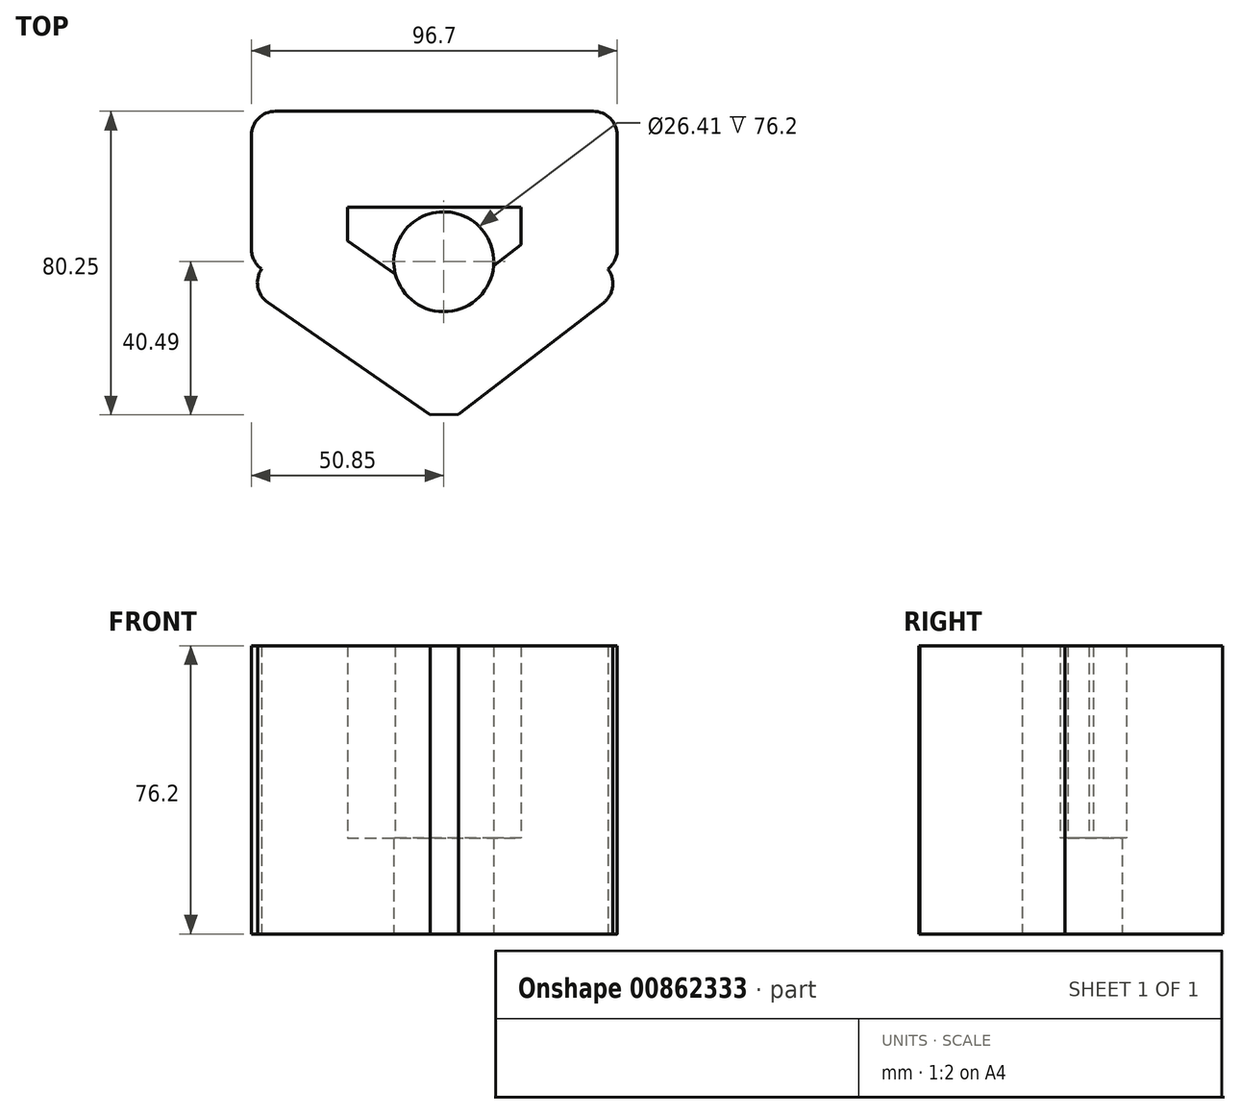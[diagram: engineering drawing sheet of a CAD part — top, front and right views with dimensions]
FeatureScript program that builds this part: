
annotation { "Feature Type Name" : "Feature", "Feature Type Description" : "" }
export const myFeature = defineFeature(function(context is Context, id is Id, definition is map)
    precondition{}
    {
        {
            var Q0;
            Q0=qCreatedBy(makeId("Top.planeOp"),FACE);
            var sketch = newSketch(context, id + "F0", { "sketchPlane" : qUnion([Q0])});
            skLineSegment(sketch, "E0", {"start": v(-44.5, 39.76) * mm, "end": v(39.5, 39.76) * mm});
            skLineSegment(sketch, "E1", {"start": v(-50.85, 33.4) * mm, "end": v(-50.85, 3.32) * mm});
            skPoint(sketch, "E2.visualSharp", {"position": v(-50.85, 39.76) * mm});
            skArc(sketch, "E2.filletArc", {"start": v(-44.5, 39.76) * mm, "mid": v(-48.99, 37.9) * mm, "end": v(-50.85, 33.4) * mm});
            skLineSegment(sketch, "E3", {"start": v(45.85, 33.4) * mm, "end": v(45.85, 3.13) * mm});
            skPoint(sketch, "E4.visualSharp", {"position": v(45.85, 39.76) * mm});
            skArc(sketch, "E4.filletArc", {"start": v(45.85, 33.4) * mm, "mid": v(44, 37.9) * mm, "end": v(39.5, 39.76) * mm});
            skLineSegment(sketch, "E5", {"start": v(-48.12, -1.9) * mm, "end": v(0, -35.27) * mm});
            skLineSegment(sketch, "E6", {"start": v(43.37, -1.9) * mm, "end": v(0, -35.27) * mm});
            skPoint(sketch, "E7.visualSharp", {"position": v(-50.85, 0) * mm});
            skArc(sketch, "E7.filletArc", {"start": v(-50.85, 3.32) * mm, "mid": v(-50.12, 0.38) * mm, "end": v(-48.12, -1.9) * mm});
            skPoint(sketch, "E8.visualSharp", {"position": v(45.85, 0) * mm});
            skArc(sketch, "E8.filletArc", {"start": v(43.37, -1.9) * mm, "mid": v(45.2, 0.32) * mm, "end": v(45.85, 3.13) * mm});
            skLineSegment(sketch, "E9.0", {"start": v(-46.52, -10.73) * mm, "end": v(-3.62, -40.49) * mm});
            skLineSegment(sketch, "E10", {"start": v(-48.12, -1.9) * mm, "end": v(-48.12, -1.9) * mm});
            skLineSegment(sketch, "E11", {"start": v(-3.62, -40.49) * mm, "end": v(0, -35.27) * mm});
            skLineSegment(sketch, "E12", {"start": v(0, -35.27) * mm, "end": v(3.73, -40.12) * mm});
            skLineSegment(sketch, "E13.0", {"start": v(42.21, -10.81) * mm, "end": v(3.87, -40.3) * mm});
            skCircle(sketch, "E14", {"center": v(0, 0) * mm, "radius": 13.2 * mm});
            skLineSegment(sketch, "E15", {"start": v(43.37, -1.9) * mm, "end": v(43.37, -1.9) * mm});
            skLineSegment(sketch, "E16", {"start": v(-3.62, -40.49) * mm, "end": v(3.87, -40.3) * mm});
            skPoint(sketch, "E17.visualSharp", {"position": v(-51.74, -7.11) * mm});
            skArc(sketch, "E17.filletArc", {"start": v(-48.12, -1.9) * mm, "mid": v(-49.15, -6.64) * mm, "end": v(-46.52, -10.73) * mm});
            skPoint(sketch, "E18.visualSharp", {"position": v(47.24, -6.94) * mm});
            skArc(sketch, "E18.filletArc", {"start": v(42.21, -10.81) * mm, "mid": v(44.64, -6.6) * mm, "end": v(43.37, -1.9) * mm});
            skSolve(sketch);
        }
        {
            var Q0;
            Q0=makeQuery(id+"F0.imprint","IMPRINT",FACE,{"disambiguationData":[TD([[makeQuery(id+"F0.imprint","IMPRINT",EDGE,{"derivedFrom":sQuery(id+"F0.wireOp",EDGE,"E0")}),-1.0]])]});
            var Q1;
            Q1=makeQuery(id+"F0.imprint","IMPRINT",FACE,{"disambiguationData":[TD([[makeQuery(id+"F0.imprint","IMPRINT",EDGE,{"derivedFrom":sQuery(id+"F0.wireOp",EDGE,"E5")}),-1.0]])]});
            var Q2;
            Q2=makeQuery(id+"F0.imprint","IMPRINT",FACE,{"disambiguationData":[TD([[makeQuery(id+"F0.imprint","IMPRINT",EDGE,{"derivedFrom":sQuery(id+"F0.wireOp",EDGE,"E6")}),1.0]])]});
            extrude(context, id + "F1", {"entities" : qUnion([Q0, Q1, Q2]), "depth" : 76.2 * mm, "offsetDistance" : 25.4 * mm});
        }
        {
            var Q0;
            Q0=makeQuery(id+"F1.opExtrude","SWEPT_FACE",FACE,{"disambiguationData":[OSD([sQuery(id+"F0.wireOp",EDGE,"E14")])]});
            var Q1;
            Q1=makeQuery(id+"F1.opExtrude","CAP_FACE",FACE,{"disambiguationData":[OSD([sQuery(id+"F0.wireOp",EDGE,"E0"),sQuery(id+"F0.wireOp",EDGE,"E1"),sQuery(id+"F0.wireOp",EDGE,"E2.filletArc"),sQuery(id+"F0.wireOp",EDGE,"E3"),sQuery(id+"F0.wireOp",EDGE,"E4.filletArc"),sQuery(id+"F0.wireOp",EDGE,"E7.filletArc"),sQuery(id+"F0.wireOp",EDGE,"E8.filletArc"),sQuery(id+"F0.wireOp",EDGE,"E9.0"),sQuery(id+"F0.wireOp",EDGE,"E13.0"),sQuery(id+"F0.wireOp",EDGE,"E14"),sQuery(id+"F0.wireOp",EDGE,"E16"),sQuery(id+"F0.wireOp",EDGE,"E17.filletArc"),sQuery(id+"F0.wireOp",EDGE,"E18.filletArc")])],"isStart":false});
            shell(context, id + "F2", {"entities" : qUnion([Q0, Q1]), "thickness" : 25.4 * mm});
        }
        {
            var Q0;
            Q0=makeQuery(id+"F2.opShell","OFFSET_FACE",FACE,{"disambiguationData":[OSD([sQuery(id+"F0.wireOp",EDGE,"E0"),sQuery(id+"F0.wireOp",EDGE,"E1"),sQuery(id+"F0.wireOp",EDGE,"E2.filletArc"),sQuery(id+"F0.wireOp",EDGE,"E3"),sQuery(id+"F0.wireOp",EDGE,"E4.filletArc"),sQuery(id+"F0.wireOp",EDGE,"E7.filletArc"),sQuery(id+"F0.wireOp",EDGE,"E8.filletArc"),sQuery(id+"F0.wireOp",EDGE,"E9.0"),sQuery(id+"F0.wireOp",EDGE,"E13.0"),sQuery(id+"F0.wireOp",EDGE,"E14"),sQuery(id+"F0.wireOp",EDGE,"E16"),sQuery(id+"F0.wireOp",EDGE,"E17.filletArc"),sQuery(id+"F0.wireOp",EDGE,"E18.filletArc")])]});
            extrude(context, id + "F3", {"entities" : qUnion([Q0]), "operationType" : NewBodyOperationType.ADD, "oppositeDirection" : true, "depth" : 25.4 * mm, "offsetDistance" : 25.4 * mm});
        }
        {
            var Q0;
            Q0=makeQuery(id+"F2.opShell","OFFSET_FACE",FACE,{"disambiguationData":[OSD([sQuery(id+"F0.wireOp",EDGE,"E0"),sQuery(id+"F0.wireOp",EDGE,"E1"),sQuery(id+"F0.wireOp",EDGE,"E2.filletArc"),sQuery(id+"F0.wireOp",EDGE,"E3"),sQuery(id+"F0.wireOp",EDGE,"E4.filletArc"),sQuery(id+"F0.wireOp",EDGE,"E7.filletArc"),sQuery(id+"F0.wireOp",EDGE,"E8.filletArc"),sQuery(id+"F0.wireOp",EDGE,"E9.0"),sQuery(id+"F0.wireOp",EDGE,"E13.0"),sQuery(id+"F0.wireOp",EDGE,"E14"),sQuery(id+"F0.wireOp",EDGE,"E16"),sQuery(id+"F0.wireOp",EDGE,"E17.filletArc"),sQuery(id+"F0.wireOp",EDGE,"E18.filletArc")])]});
            extrude(context, id + "F4", {"entities" : qUnion([Q0]), "operationType" : NewBodyOperationType.ADD, "oppositeDirection" : true, "depth" : 25.4 * mm, "offsetDistance" : 25.4 * mm});
        }
        {
            var Q0;
            Q0=makeQuery(id+"F2.opShell","OFFSET_FACE",FACE,{"disambiguationData":[OSD([sQuery(id+"F0.wireOp",EDGE,"E0"),sQuery(id+"F0.wireOp",EDGE,"E1"),sQuery(id+"F0.wireOp",EDGE,"E2.filletArc"),sQuery(id+"F0.wireOp",EDGE,"E3"),sQuery(id+"F0.wireOp",EDGE,"E4.filletArc"),sQuery(id+"F0.wireOp",EDGE,"E7.filletArc"),sQuery(id+"F0.wireOp",EDGE,"E8.filletArc"),sQuery(id+"F0.wireOp",EDGE,"E9.0"),sQuery(id+"F0.wireOp",EDGE,"E13.0"),sQuery(id+"F0.wireOp",EDGE,"E14"),sQuery(id+"F0.wireOp",EDGE,"E16"),sQuery(id+"F0.wireOp",EDGE,"E17.filletArc"),sQuery(id+"F0.wireOp",EDGE,"E18.filletArc")])]});
            extrude(context, id + "F5", {"entities" : qUnion([Q0]), "operationType" : NewBodyOperationType.ADD, "depth" : -25.4 * mm, "offsetDistance" : 25.4 * mm});
        }
        {
            var Q0;
            Q0=makeQuery(id+"F2.opShell","OFFSET_FACE",FACE,{"disambiguationData":[OSD([sQuery(id+"F0.wireOp",EDGE,"E0"),sQuery(id+"F0.wireOp",EDGE,"E1"),sQuery(id+"F0.wireOp",EDGE,"E2.filletArc"),sQuery(id+"F0.wireOp",EDGE,"E3"),sQuery(id+"F0.wireOp",EDGE,"E4.filletArc"),sQuery(id+"F0.wireOp",EDGE,"E7.filletArc"),sQuery(id+"F0.wireOp",EDGE,"E8.filletArc"),sQuery(id+"F0.wireOp",EDGE,"E9.0"),sQuery(id+"F0.wireOp",EDGE,"E13.0"),sQuery(id+"F0.wireOp",EDGE,"E14"),sQuery(id+"F0.wireOp",EDGE,"E16"),sQuery(id+"F0.wireOp",EDGE,"E17.filletArc"),sQuery(id+"F0.wireOp",EDGE,"E18.filletArc")])]});
            extrude(context, id + "F6", {"entities" : qUnion([Q0]), "operationType" : NewBodyOperationType.ADD, "depth" : -25.4 * mm, "offsetDistance" : 25.4 * mm});
        }
    });
